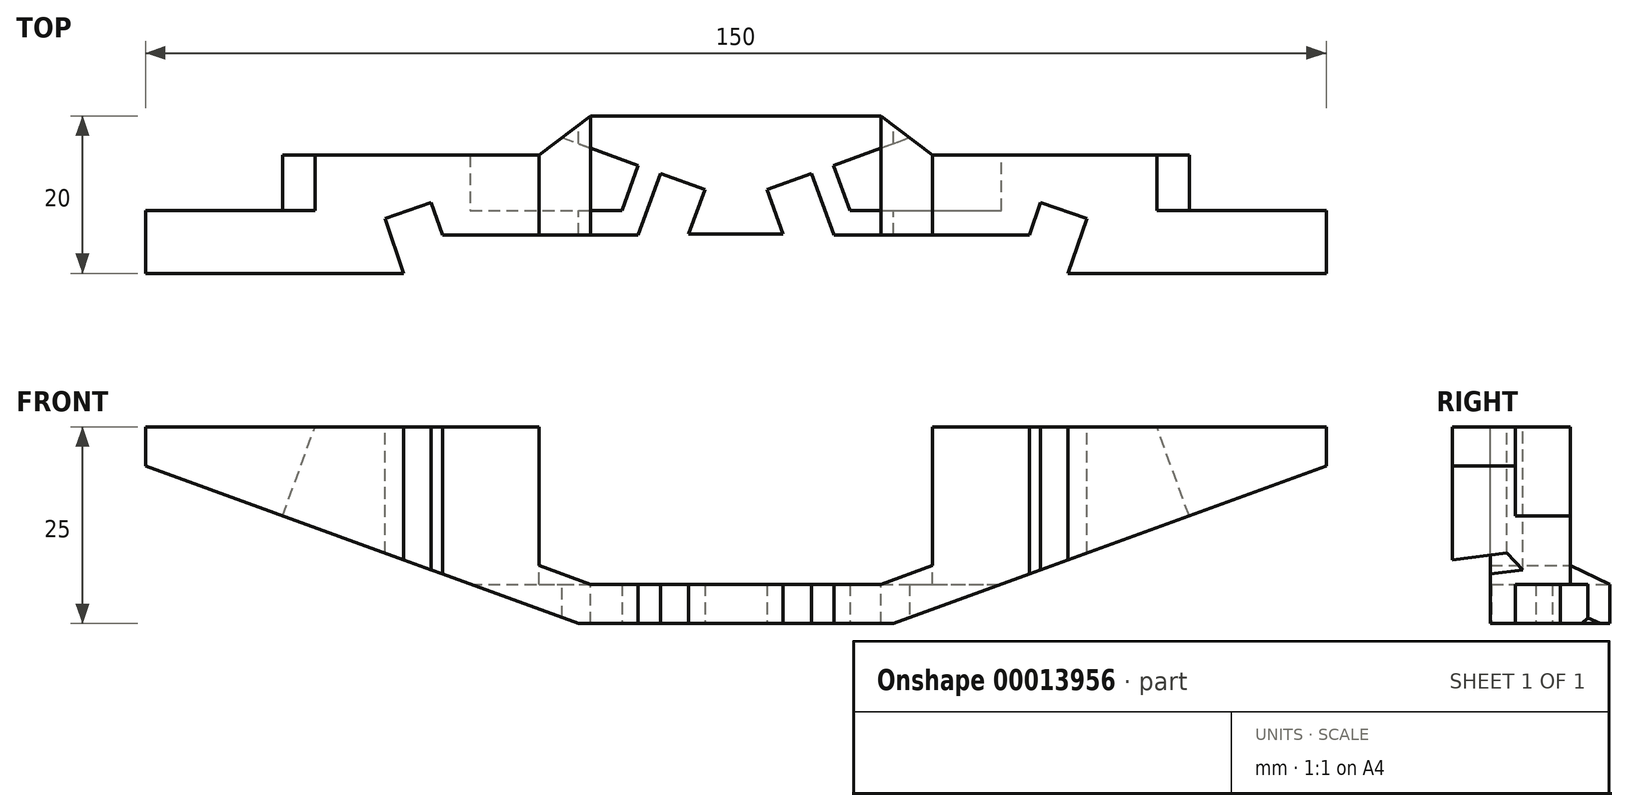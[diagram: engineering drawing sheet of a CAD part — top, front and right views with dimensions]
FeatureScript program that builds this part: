
annotation { "Feature Type Name" : "Feature", "Feature Type Description" : "" }
export const myFeature = defineFeature(function(context is Context, id is Id, definition is map)
    precondition{}
    {
        {
            var Q0;
            Q0=qCreatedBy(makeId("Front.planeOp"),FACE);
            var sketch = newSketch(context, id + "F0", { "sketchPlane" : qUnion([Q0])});
            skLineSegment(sketch, "E0", {"start": v(20, 0) * mm, "end": v(-20, 0) * mm});
            skLineSegment(sketch, "E1", {"start": v(-20, 0) * mm, "end": v(-75, 20.02) * mm});
            skLineSegment(sketch, "E2", {"start": v(-75, 20.02) * mm, "end": v(-75, 25) * mm});
            skLineSegment(sketch, "E3", {"start": v(75, 25) * mm, "end": v(75, 20.02) * mm});
            skLineSegment(sketch, "E4", {"start": v(75, 20.02) * mm, "end": v(20, 0) * mm});
            skPoint(sketch, "E5", {"position": v(0, 0) * mm});
            skLineSegment(sketch, "E6", {"start": v(-25, 25) * mm, "end": v(-25, 7.38) * mm});
            skLineSegment(sketch, "E7", {"start": v(-25, 7.38) * mm, "end": v(-18.45, 5) * mm});
            skLineSegment(sketch, "E8", {"start": v(-18.45, 5) * mm, "end": v(18.45, 5) * mm});
            skLineSegment(sketch, "E9", {"start": v(18.45, 5) * mm, "end": v(25, 7.38) * mm});
            skLineSegment(sketch, "E10", {"start": v(25, 7.38) * mm, "end": v(25, 25) * mm});
            skLineSegment(sketch, "E11", {"start": v(-75, 25) * mm, "end": v(-25, 25) * mm});
            skLineSegment(sketch, "E12", {"start": v(25, 25) * mm, "end": v(75, 25) * mm});
            skSolve(sketch);
        }
        {
            var Q0;
            Q0=makeQuery(id+"F0.imprint","IMPRINT",FACE,{"disambiguationData":[TD([[makeQuery(id+"F0.imprint","IMPRINT",EDGE,{"derivedFrom":sQuery(id+"F0.wireOp",EDGE,"E0")}),-1.0]])]});
            extrude(context, id + "F1", {"entities" : qUnion([Q0]), "depth" : 20 * mm});
        }
        {
            var Q0;
            Q0=makeQuery(id+"F1.opExtrude","SWEPT_FACE",FACE,{"disambiguationData":[OSD([sQuery(id+"F0.wireOp",EDGE,"E11")])]});
            cPlane(context, id + "F2", {"entities" : qUnion([Q0]), "cplaneType" : CPlaneType.OFFSET, "offset" : 0 * mm, "width" : 150 * mm, "height" : 150 * mm});
        }
        {
            var Q0;
            Q0=qCreatedBy(id+"F2.planeOp",FACE);
            var sketch = newSketch(context, id + "F3", { "sketchPlane" : qUnion([Q0])});
            skLineSegment(sketch, "E13", {"start": v(-75, -5) * mm, "end": v(-25, -5) * mm});
            skLineSegment(sketch, "E14", {"start": v(-25, -5) * mm, "end": v(-18.45, 0) * mm});
            skLineSegment(sketch, "E15", {"start": v(-18.45, 0) * mm, "end": v(-75, 0) * mm});
            skLineSegment(sketch, "E16", {"start": v(75, 0) * mm, "end": v(18.45, 0) * mm});
            skLineSegment(sketch, "E17", {"start": v(18.45, 0) * mm, "end": v(25, -5) * mm});
            skLineSegment(sketch, "E18", {"start": v(25, -5) * mm, "end": v(75, -5) * mm});
            skLineSegment(sketch, "E19", {"start": v(75, -5) * mm, "end": v(75, -5) * mm});
            skLineSegment(sketch, "E20", {"start": v(75, -5) * mm, "end": v(75, 0) * mm});
            skLineSegment(sketch, "E21", {"start": v(-75, -5) * mm, "end": v(-75, 0) * mm});
            skSolve(sketch);
        }
        {
            var Q0;
            Q0=makeQuery(id+"F3.imprint","IMPRINT",FACE,{"disambiguationData":[TD([[makeQuery(id+"F3.imprint","IMPRINT",EDGE,{"derivedFrom":sQuery(id+"F3.wireOp",EDGE,"4a7f2df4-24a0-4489-a68b-77bac6bcb06e")}),1.0]])]});
            var Q1;
            Q1 = qSketchRegion(id + "F3", true);
            extrude(context, id + "F4", {"entities" : qUnion([Q0, Q1]), "operationType" : NewBodyOperationType.REMOVE, "oppositeDirection" : true, "depth" : 25 * mm});
        }
        {
            var Q0;
            Q0=makeQuery(id+"F4.boolean.opBoolean","COPY",FACE,{"derivedFrom":makeQuery(id+"F4.opExtrude","SWEPT_FACE",FACE,{"disambiguationData":[OSD([sQuery(id+"F3.wireOp",EDGE,"E13")])]})});
            var sketch = newSketch(context, id + "F5", { "sketchPlane" : qUnion([Q0])});
            skLineSegment(sketch, "E22", {"start": v(57.59, 13.68) * mm, "end": v(53.47, 25) * mm});
            skLineSegment(sketch, "E23", {"start": v(53.47, 25) * mm, "end": v(75, 25) * mm});
            skLineSegment(sketch, "E24", {"start": v(75, 25) * mm, "end": v(75, 20.02) * mm});
            skLineSegment(sketch, "E25", {"start": v(75, 20.02) * mm, "end": v(57.59, 13.68) * mm});
            skSolve(sketch);
        }
        {
            var Q0;
            Q0=makeQuery(id+"F5.imprint","IMPRINT",FACE,{"disambiguationData":[TD([[makeQuery(id+"F5.imprint","IMPRINT",EDGE,{"derivedFrom":sQuery(id+"F5.wireOp",EDGE,"E22")}),-1.0]])]});
            extrude(context, id + "F6", {"entities" : qUnion([Q0]), "oppositeDirection" : true, "depth" : 7 * mm});
        }
        {
            var Q0;
            Q0=makeQuery(id+"F6.opExtrude","SWEPT_BODY",BODY,{"disambiguationData":[OSD([sQuery(id+"F5.wireOp",EDGE,"E22"),sQuery(id+"F5.wireOp",EDGE,"E23"),sQuery(id+"F5.wireOp",EDGE,"E24"),sQuery(id+"F5.wireOp",EDGE,"E25")])]});
            var Q1;
            Q1=qCreatedBy(makeId("Right.planeOp"),FACE);
            mirror(context, id + "F7", {"entities" : qUnion([Q0]), "mirrorPlane" : qUnion([Q1])});
        }
        {
            var Q0;
            Q0=makeQuery(id+"F6.opExtrude","SWEPT_BODY",BODY,{"disambiguationData":[OSD([sQuery(id+"F5.wireOp",EDGE,"E22"),sQuery(id+"F5.wireOp",EDGE,"E23"),sQuery(id+"F5.wireOp",EDGE,"E24"),sQuery(id+"F5.wireOp",EDGE,"E25")])]});
            var Q1;
            Q1=makeQuery(id+"F7.opPattern","COPY",BODY,{"derivedFrom":makeQuery(id+"F6.opExtrude","SWEPT_BODY",BODY,{"disambiguationData":[OSD([sQuery(id+"F5.wireOp",EDGE,"E22"),sQuery(id+"F5.wireOp",EDGE,"E23"),sQuery(id+"F5.wireOp",EDGE,"E24"),sQuery(id+"F5.wireOp",EDGE,"E25")])]}),"instanceName":"1"});
            var Q2;
            Q2=makeQuery(id+"F1.opExtrude","SWEPT_BODY",BODY,{"disambiguationData":[OSD([sQuery(id+"F0.wireOp",EDGE,"E0"),sQuery(id+"F0.wireOp",EDGE,"E1"),sQuery(id+"F0.wireOp",EDGE,"E2"),sQuery(id+"F0.wireOp",EDGE,"E3"),sQuery(id+"F0.wireOp",EDGE,"E4"),sQuery(id+"F0.wireOp",EDGE,"E6"),sQuery(id+"F0.wireOp",EDGE,"E7"),sQuery(id+"F0.wireOp",EDGE,"E8"),sQuery(id+"F0.wireOp",EDGE,"E9"),sQuery(id+"F0.wireOp",EDGE,"E10"),sQuery(id+"F0.wireOp",EDGE,"E11"),sQuery(id+"F0.wireOp",EDGE,"E12")])]});
            booleanBodies(context, id + "F8", {"operationType" : BooleanOperationType.SUBTRACTION, "tools" : qUnion([Q0, Q1]), "targets" : qUnion([Q2])});
        }
        {
            var Q0;
            Q0=makeQuery(id+"F1.opExtrude","SWEPT_FACE",FACE,{"disambiguationData":[OSD([sQuery(id+"F0.wireOp",EDGE,"E0")])]});
            var sketch = newSketch(context, id + "F9", { "sketchPlane" : qUnion([Q0])});
            skLineSegment(sketch, "E26", {"start": v(6, 15) * mm, "end": v(-6, 15) * mm});
            skPoint(sketch, "E27", {"position": v(0, 15) * mm});
            skLineSegment(sketch, "E28", {"start": v(-6, 15) * mm, "end": v(-3.95, 9.36) * mm});
            skLineSegment(sketch, "E29", {"start": v(-3.95, 9.36) * mm, "end": v(-9.59, 7.3) * mm});
            skLineSegment(sketch, "E30", {"start": v(-9.59, 7.3) * mm, "end": v(-14.2, 20) * mm});
            skLineSegment(sketch, "E31", {"start": v(-14.2, 20) * mm, "end": v(14.2, 20) * mm});
            skLineSegment(sketch, "E32", {"start": v(14.2, 20) * mm, "end": v(9.59, 7.3) * mm});
            skLineSegment(sketch, "E33", {"start": v(9.59, 7.3) * mm, "end": v(3.95, 9.36) * mm});
            skLineSegment(sketch, "E34", {"start": v(3.95, 9.36) * mm, "end": v(6, 15) * mm});
            skLineSegment(sketch, "E35", {"start": v(-57.59, 12) * mm, "end": v(-14.49, 12) * mm});
            skLineSegment(sketch, "E36", {"start": v(14.49, 12) * mm, "end": v(57.59, 12) * mm});
            skLineSegment(sketch, "E37", {"start": v(-29.67, 0) * mm, "end": v(-12.4, 6.28) * mm});
            skLineSegment(sketch, "E38", {"start": v(12.4, 6.28) * mm, "end": v(29.67, 0) * mm});
            skLineSegment(sketch, "E39", {"start": v(-12.4, 6.28) * mm, "end": v(-14.49, 12) * mm});
            skLineSegment(sketch, "E40", {"start": v(12.4, 6.28) * mm, "end": v(14.49, 12) * mm});
            skLineSegment(sketch, "E41", {"start": v(-57.59, 12) * mm, "end": v(-57.59, 0) * mm});
            skLineSegment(sketch, "E42", {"start": v(-57.59, 0) * mm, "end": v(-29.67, 0) * mm});
            skLineSegment(sketch, "E43", {"start": v(29.67, 0) * mm, "end": v(57.59, 0) * mm});
            skLineSegment(sketch, "E44", {"start": v(57.59, 12) * mm, "end": v(57.59, 0) * mm});
            skSolve(sketch);
        }
        {
            var Q0;
            Q0 = qSketchRegion(id + "F9", true);
            extrude(context, id + "F10", {"entities" : qUnion([Q0]), "operationType" : NewBodyOperationType.REMOVE, "oppositeDirection" : true, "depth" : 5 * mm});
        }
        {
            var Q0;
            Q0=qCreatedBy(id+"F2.planeOp",FACE);
            var sketch = newSketch(context, id + "F11", { "sketchPlane" : qUnion([Q0])});
            skLineSegment(sketch, "E45", {"start": v(38.7, -11.01) * mm, "end": v(44.58, -13.04) * mm});
            skLineSegment(sketch, "E46", {"start": v(44.58, -13.04) * mm, "end": v(42.17, -20.02) * mm});
            skLineSegment(sketch, "E47", {"start": v(12.43, -15.13) * mm, "end": v(37.27, -15.13) * mm});
            skPoint(sketch, "E47.startSnap0", {"position": v(36.7, -15.13) * mm});
            skLineSegment(sketch, "E48", {"start": v(12.43, -15.13) * mm, "end": v(14.21, -20.02) * mm});
            skLineSegment(sketch, "E49", {"start": v(14.21, -20.02) * mm, "end": v(42.17, -20.02) * mm});
            skLineSegment(sketch, "E50", {"start": v(37.27, -15.13) * mm, "end": v(38.7, -11.01) * mm});
            skPoint(sketch, "E51.orphan", {"position": v(32.81, -8.98) * mm});
            skLineSegment(sketch, "E52.MirrorCS", {"start": v(-38.7, -11.01) * mm, "end": v(-44.58, -13.04) * mm});
            skPoint(sketch, "E53.MirrorP", {"position": v(-32.81, -8.98) * mm});
            skLineSegment(sketch, "E54.MirrorCS", {"start": v(-37.27, -15.13) * mm, "end": v(-38.7, -11.01) * mm});
            skPoint(sketch, "E55.MirrorP", {"position": v(-36.7, -15.13) * mm});
            skLineSegment(sketch, "E56.MirrorCS", {"start": v(-12.43, -15.13) * mm, "end": v(-37.27, -15.13) * mm});
            skLineSegment(sketch, "E57.MirrorCS", {"start": v(-14.21, -20.02) * mm, "end": v(-42.17, -20.02) * mm});
            skLineSegment(sketch, "E58.MirrorCS", {"start": v(-12.43, -15.13) * mm, "end": v(-14.21, -20.02) * mm});
            skLineSegment(sketch, "E59.MirrorCS", {"start": v(-44.58, -13.04) * mm, "end": v(-42.17, -20.02) * mm});
            skSolve(sketch);
        }
        {
            var Q0;
            Q0=makeQuery(id+"F11.imprint","IMPRINT",FACE,{"disambiguationData":[TD([[makeQuery(id+"F11.imprint","IMPRINT",EDGE,{"derivedFrom":sQuery(id+"F11.wireOp",EDGE,"E52.MirrorCS")}),1.0]])]});
            var Q1;
            Q1=makeQuery(id+"F11.imprint","IMPRINT",FACE,{"disambiguationData":[TD([[makeQuery(id+"F11.imprint","IMPRINT",EDGE,{"derivedFrom":sQuery(id+"F11.wireOp",EDGE,"E45")}),-1.0]])]});
            extrude(context, id + "F12", {"entities" : qUnion([Q0, Q1]), "operationType" : NewBodyOperationType.REMOVE, "endBound" : BoundingType.THROUGH_ALL, "oppositeDirection" : true, "depth" : 25 * mm});
        }
    });
